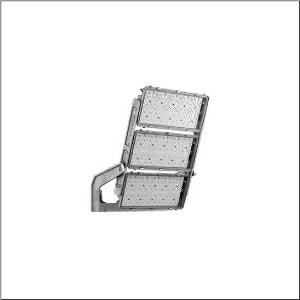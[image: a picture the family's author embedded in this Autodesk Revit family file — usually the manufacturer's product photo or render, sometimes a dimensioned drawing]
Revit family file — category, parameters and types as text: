
# Revit family: floodlight_fl_11_maxi_pro_remote___pl64_5xa779524e01ba_e2b2
name_source: partatom
category: Lighting Fixtures
units: mm (PartAtom-declared; Revit-internal decimal feet)

## family parameters
Cut with Voids When Loaded = No
Host = Face
Light Source = No
Part Type = Normal
Room Calculation Point = No
Round Connector Dimension = Use Diameter
Shared = No

## types (1)
- --- (1 x LED, 107650 lm, 1020.5 W, 5700K)
    Apparent Load = 1020 VA
    CIE Flux Codes = 28 80 98 100 100
    Color Rendering = 90
    Color Temperature = 5700K
    Default Elevation = 1800 mm
    Description = Floodlight FL 11  maxi  pro Remote floodlight; light control with lens of PMMA; cover panel of toughened safety glass, transparent; light distribution: PL64, asymmetric direct distribution, LEDcolour temperature: 5700K, rated luminous flux: 107.650lm, colour rendering: CRI > 90, light colour: 957; luminous efficacy: 106lm/W; brightness control: DMX+RDM; with terminal, 8-pole, max. 2.5mm², mains connection: 220..240V/380..400V AC, 50/60Hz, surge voltage resistance: line to ground: 10kV, ECG replaceable separately, LED unit replaceable without ESD environment, dustproof LED module, dimming range 10..100%; 1021W floodlight with 3x LED unit of diecast aluminium, coated grey; length: 713mm / width: 651mm / height: 338mm; mounting bracket, of diecast aluminium, uncoated, natural, equipment: Longlife, protection rating (complete): IP66; insulation class (complete): insulation class I (protective earthing); certification: CE, ENEC, VDE; ball protection: ball impact resistance with accessories, impact resistance: IK07; only for outdoor installations, rated ambient temperature 10°C, permissible operating ambient temperature: -40..+40°C, permissible storage temperature: -40..+85°Cpackaging unit: 1 piece

Light Distribution: PL64
    Height = 320 mm
    Lamp = 1 x LED
    Lamp Light Flux = 107650 lm
    Lamp Power = 1020.5 W
    Lamp count = 1
    Length = 1002 mm
    Luminous efficacy = 105 lm/W
    Manufacturer = Siteco
    ModVariant = No
    Model = 5XA779524E01BA
    Mounting Place = Ceiling
    Mounting Type = Surface mounted
    Number of Poles = 1
    OnlyDefault = Yes
    Power Factor = 1
    Product Name = Floodlight FL 11 maxi pro Remote | PL64
    Product group = floodlight | ceiling mounted
    ProductGroupID = 301
    Protection Class = Protection class I
    Protection Degree = IP 66
    RLX_Detail_Level = 1
    RLX_Emergency_Light_Flux = 0 lm
    RLX_Emergency_Type = 0
    RLX_Emergency_Type_DB = No
    RlxData = <blob elided: 52461 chars, md5=e6e7b55c>
    Socket = socket
    Standby Power = 0 W
    System Light Flux = 107650 lm
    System Power = 1020 W
    Type Comments = factory setting: luminous flux: 100 % | dim-lin: 255 | 710 mA
    Type Image = l_1349141.jpg
    URL = http://relux.com
    VarID = @adj_097272
    Voltage = 0 V
    Weight = 0.00 kg
    Width = 655 mm

## geometry (parser evidence)
native form markers: Blend x4, Sweep x13
no freeform markers — native parametric forms only
